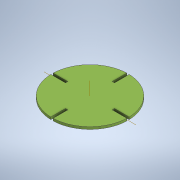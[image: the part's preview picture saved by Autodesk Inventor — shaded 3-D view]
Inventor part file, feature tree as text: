
AUTODESK INVENTOR PART (.ipt)
format: ipt  version: 2021 (Build 250183000, 183)  size: 139,264 bytes
history: native  units: in
note: dims shown in document units (in); Inventor stores cm internally (conversion verified against a paired STEP export)
features: sketch x2, other x2, extrude x1
ambient origin geometry x8: Origin, YZ Plane, XZ Plane, XY Plane, X Axis, Y Axis, Z Axis, Center Point
bodies: Solid1 (feature_tree)
feature tree (5):
  sketch  "Sketch1"  dims[d2=0.0315in d3=0.0315in]
  extrude  "Extrusion1"  Depth=0.0315in
  other  "Work Axis1"
  other  "Work Axis2"
  sketch  "Sketch2"  dims[d4=0.0315in d5=0.0315in d6=1.2598in d7=0.0in d8=0.0in d9=2.0472in d10=0.0in d11=0.0in d12=0.0in d13=0.063in d14=0.0in d15=0.5942in]
